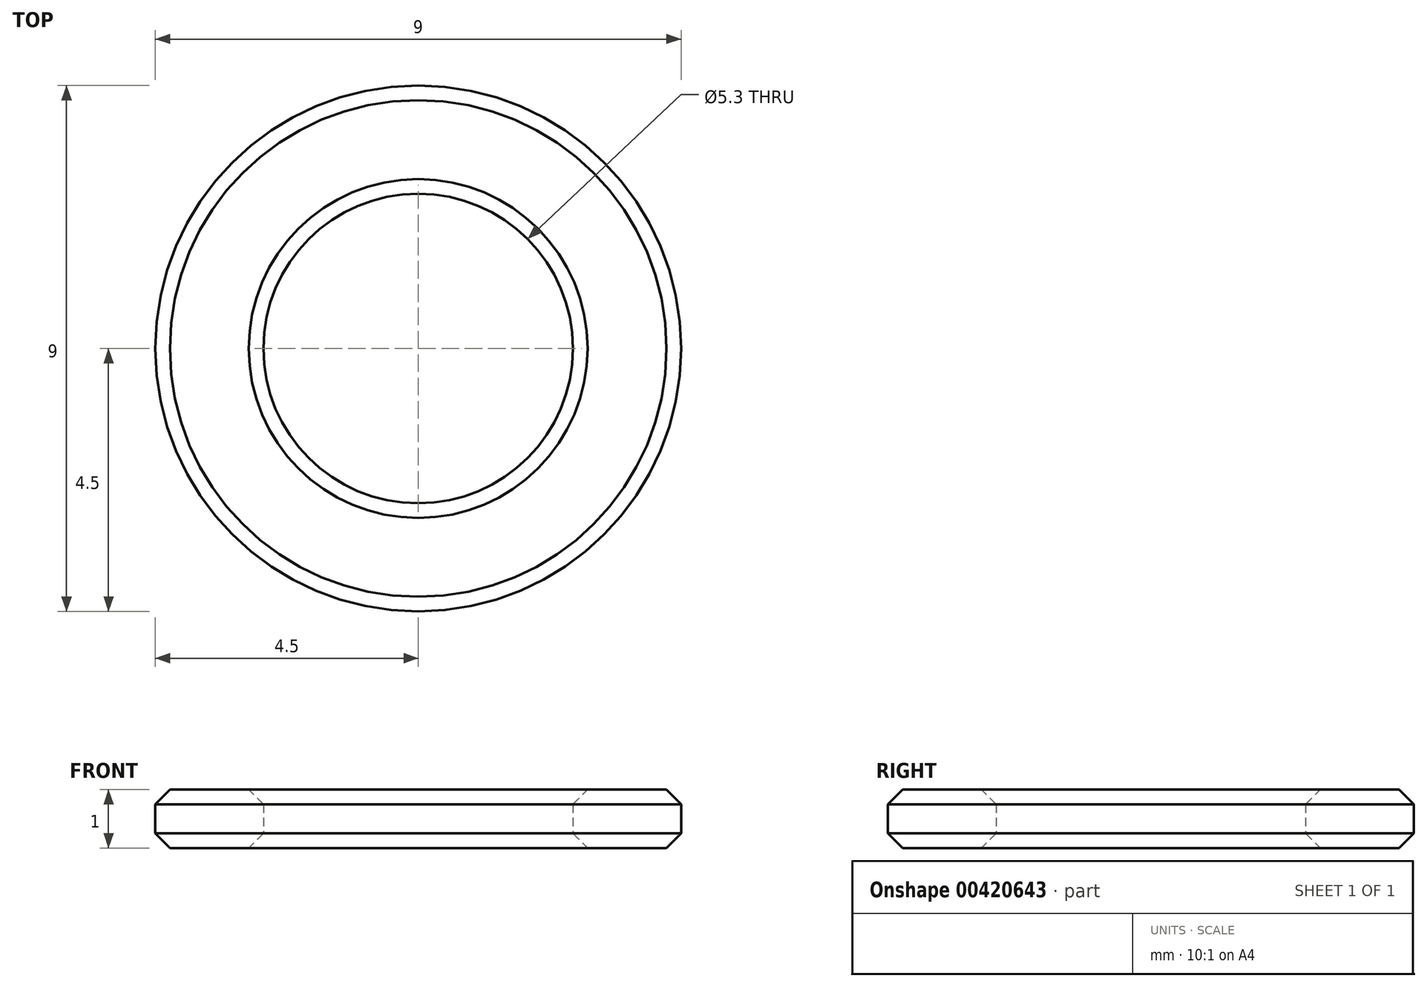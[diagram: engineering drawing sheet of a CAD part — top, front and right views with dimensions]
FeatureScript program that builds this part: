
annotation { "Feature Type Name" : "Feature", "Feature Type Description" : "" }
export const myFeature = defineFeature(function(context is Context, id is Id, definition is map)
    precondition{}
    {
        {
            var Q0;
            Q0=qCreatedBy(makeId("Top.planeOp"),FACE);
            var sketch = newSketch(context, id + "F0", { "sketchPlane" : qUnion([Q0])});
            skCircle(sketch, "E0", {"center": v(0, 0) * mm, "radius": 4.5 * mm});
            skCircle(sketch, "E1", {"center": v(0, 0) * mm, "radius": 2.65 * mm});
            skSolve(sketch);
        }
        {
            var Q0;
            Q0=makeQuery(id+"F0.imprint","IMPRINT",FACE,{"disambiguationData":[TD([[makeQuery(id+"F0.imprint","IMPRINT",EDGE,{"derivedFrom":sQuery(id+"F0.wireOp",EDGE,"E0")}),1.0]])]});
            extrude(context, id + "F1", {"entities" : qUnion([Q0]), "depth" : 1 * mm, "offsetDistance" : 25 * mm, "symmetric" : true});
        }
        {
            var Q0;
            Q0=makeQuery(id+"F1.opExtrude","CAP_EDGE",EDGE,{"disambiguationData":[OSD([sQuery(id+"F0.wireOp",EDGE,"E0")])],"isStart":false});
            var Q1;
            Q1=makeQuery(id+"F1.opExtrude","CAP_EDGE",EDGE,{"disambiguationData":[OSD([sQuery(id+"F0.wireOp",EDGE,"E0")])],"isStart":true});
            var Q2;
            Q2=makeQuery(id+"F1.opExtrude","CAP_EDGE",EDGE,{"disambiguationData":[OSD([sQuery(id+"F0.wireOp",EDGE,"E1")])],"isStart":false});
            var Q3;
            Q3=makeQuery(id+"F1.opExtrude","CAP_EDGE",EDGE,{"disambiguationData":[OSD([sQuery(id+"F0.wireOp",EDGE,"E1")])],"isStart":true});
            chamfer(context, id + "F2", {"entities" : qUnion([Q0, Q1, Q2, Q3]), "width" : 0.25 * mm, "tangentPropagation" : true});
        }
    });
